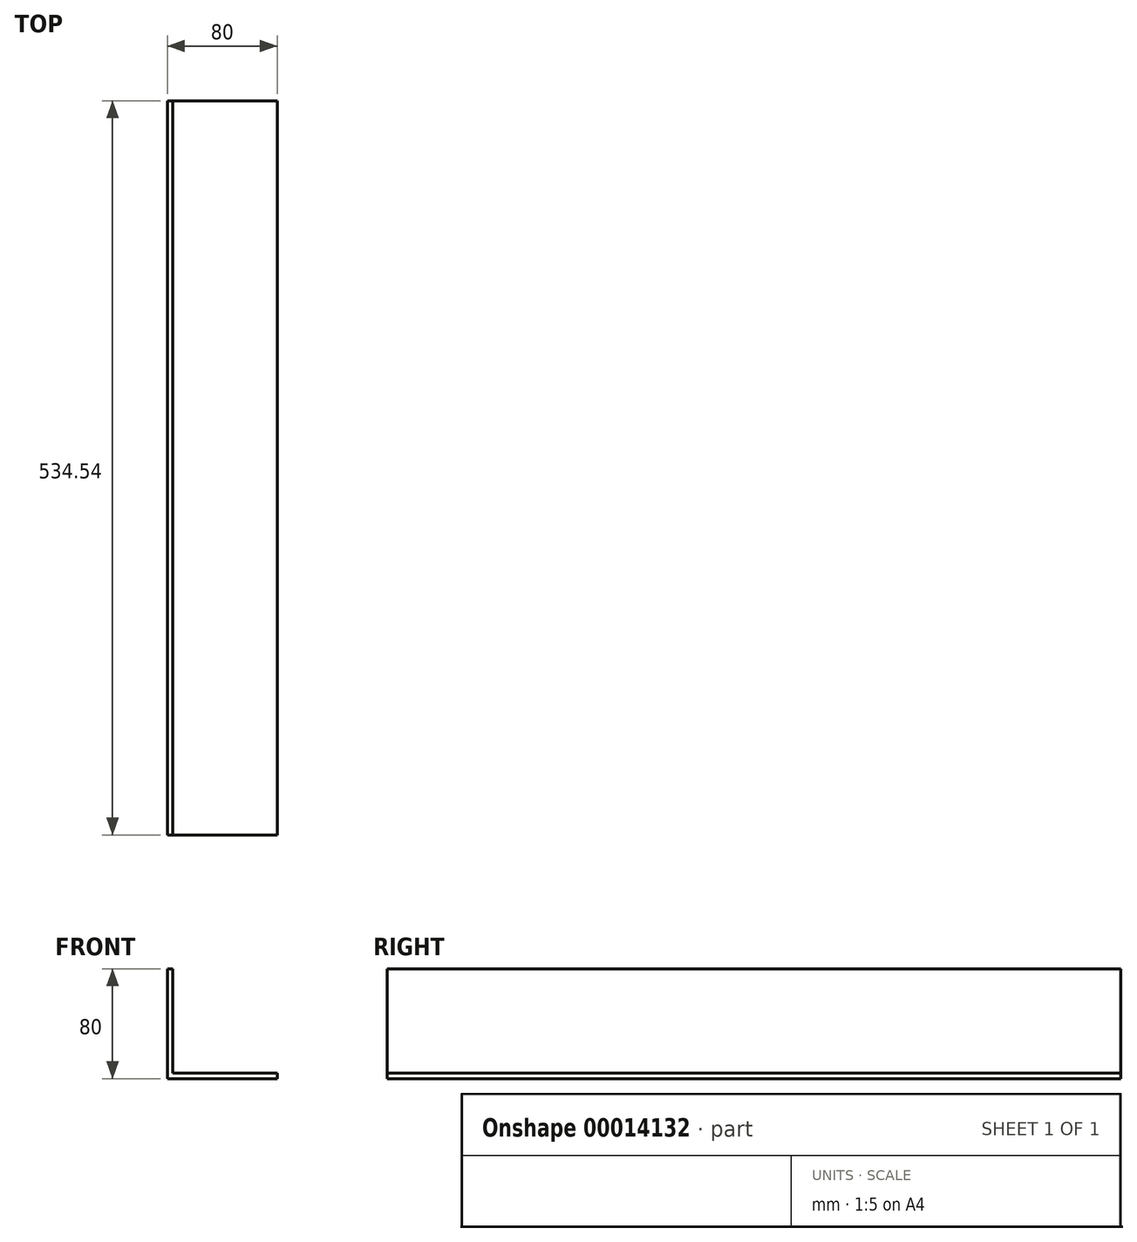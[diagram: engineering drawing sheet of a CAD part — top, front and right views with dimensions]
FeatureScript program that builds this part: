
annotation { "Feature Type Name" : "Feature", "Feature Type Description" : "" }
export const myFeature = defineFeature(function(context is Context, id is Id, definition is map)
    precondition{}
    {
        {
            var Q0;
            Q0=qCreatedBy(makeId("Front.planeOp"),FACE);
            var sketch = newSketch(context, id + "F0", { "sketchPlane" : qUnion([Q0])});
            skLineSegment(sketch, "E0.bottom", {"start": v(0, 0) * mm, "end": v(80, 0) * mm});
            skLineSegment(sketch, "E0.top", {"start": v(0, 80) * mm, "end": v(80, 80) * mm});
            skLineSegment(sketch, "E0.left", {"start": v(0, 0) * mm, "end": v(0, 80) * mm});
            skLineSegment(sketch, "E0.right", {"start": v(80, 0) * mm, "end": v(80, 80) * mm});
            skSolve(sketch);
        }
        {
            var Q0;
            Q0=qSketchRegion(id+"F0",true);
            extrude(context, id + "F1", {"entities" : qUnion([Q0]), "endBound" : BoundingType.SYMMETRIC, "depth" : 534.53 * mm});
        }
        {
            var Q0;
            Q0=makeQuery(id+"F1.opExtrude","SWEPT_FACE",FACE,{"disambiguationData":[OSD([sQuery(id+"F0.wireOp",EDGE,"E0.top")])]});
            var Q1;
            Q1=makeQuery(id+"F1.opExtrude","SWEPT_FACE",FACE,{"disambiguationData":[OSD([sQuery(id+"F0.wireOp",EDGE,"E0.right")])]});
            var Q2;
            Q2=makeQuery(id+"F1.opExtrude","CAP_FACE",FACE,{"disambiguationData":[OSD([sQuery(id+"F0.wireOp",EDGE,"E0.bottom"),sQuery(id+"F0.wireOp",EDGE,"E0.top"),sQuery(id+"F0.wireOp",EDGE,"E0.left"),sQuery(id+"F0.wireOp",EDGE,"E0.right")])],"isStart":false});
            var Q3;
            Q3=makeQuery(id+"F1.opExtrude","CAP_FACE",FACE,{"disambiguationData":[OSD([sQuery(id+"F0.wireOp",EDGE,"E0.bottom"),sQuery(id+"F0.wireOp",EDGE,"E0.top"),sQuery(id+"F0.wireOp",EDGE,"E0.left"),sQuery(id+"F0.wireOp",EDGE,"E0.right")])],"isStart":true});
            shell(context, id + "F2", {"entities" : qUnion([Q0, Q1, Q2, Q3]), "thickness" : 4 * mm});
        }
    });
